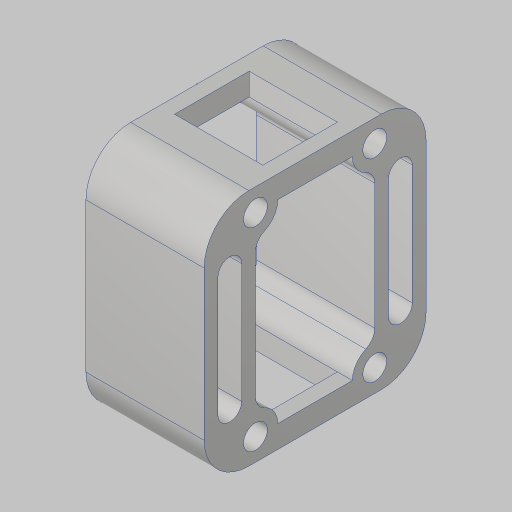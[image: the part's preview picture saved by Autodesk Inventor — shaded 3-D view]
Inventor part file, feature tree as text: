
AUTODESK INVENTOR PART (.ipt)
format: ipt  version: 2023.5 (Build 275446000, 446)  size: 199,680 bytes
history: native  units: in
note: dims shown in document units (in); Inventor stores cm internally (conversion verified against a paired STEP export)
features: sketch x3, extrude x2, fillet x2, hole x1
ambient origin geometry x8: Origin, YZ Plane, XZ Plane, XY Plane, X Axis, Y Axis, Z Axis, Center Point
bodies: Solid1 (feature_tree)
feature tree (8):
  sketch  "Sketch1"  dims[d0=1.0in d1=1.625in]
  extrude  "Extrusion1"  Depth=1.625in
  hole  "Hole1"  [1 undecoded]
  sketch  "Sketch2"  dims[d2=0.375in d3=1.86in]
  extrude  "Extrusion2"  Depth=1.0in
  fillet  "Fillet1"  Radius=0.99in
  fillet  "Fillet2"  Radius=0.125in
  sketch  "Sketch3"  dims[d4=0.1in d5=1.0in d6=0.99in d7=0.0in d8=0.201in d9=0.75in d10=0.385in d11=0.25in d12=0.5635in d13=1.0in d14=0.8108in d16=0.125in d17=0.1253in d19=0.0in d20=0.0in d21=0.125in d22=0.375in]
note: 1 required parameter value undecoded (feature->parameter linkage not recoverable at this tier; creation-order binding heuristic only, values carry confidence <= 0.55)
